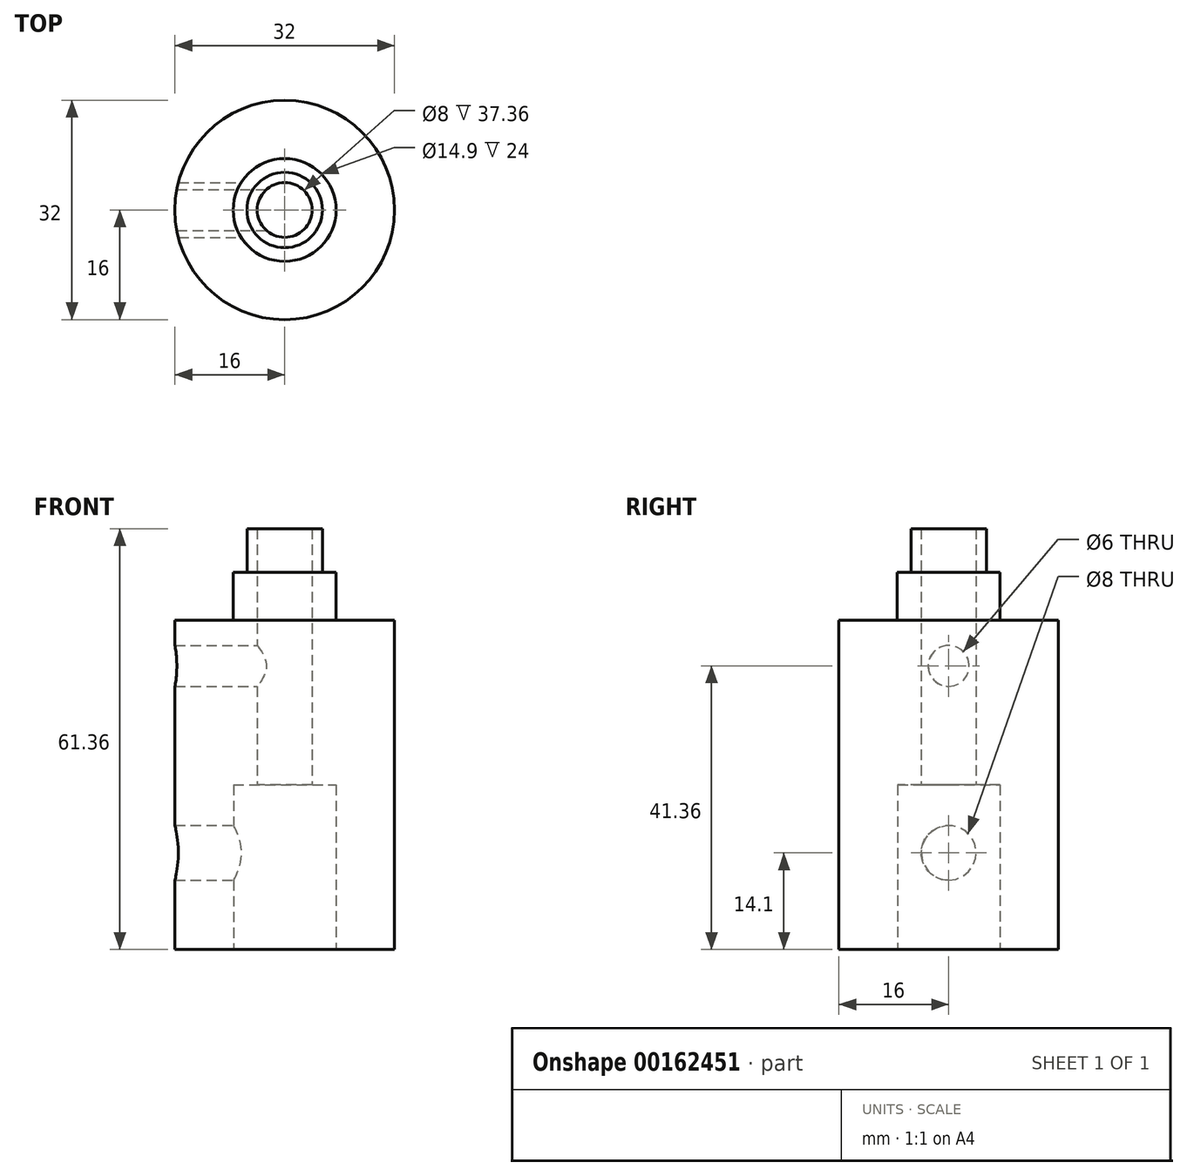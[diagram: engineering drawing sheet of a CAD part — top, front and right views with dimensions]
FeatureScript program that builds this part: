
annotation { "Feature Type Name" : "Feature", "Feature Type Description" : "" }
export const myFeature = defineFeature(function(context is Context, id is Id, definition is map)
    precondition{}
    {
        {
            var Q0;
            Q0=qCreatedBy(makeId("Top.planeOp"),FACE);
            var sketch = newSketch(context, id + "F0", { "sketchPlane" : qUnion([Q0])});
            skCircle(sketch, "E0", {"center": v(0, 0) * mm, "radius": 4 * mm});
            skCircle(sketch, "E1", {"center": v(0, 0) * mm, "radius": 5.5 * mm});
            skSolve(sketch);
        }
        {
            var Q0;
            Q0=makeQuery(id+"F0.imprint","IMPRINT",FACE,{"disambiguationData":[TD([[makeQuery(id+"F0.imprint","IMPRINT",EDGE,{"derivedFrom":sQuery(id+"F0.wireOp",EDGE,"E0")}),-1.0]])]});
            extrude(context, id + "F1", {"entities" : qUnion([Q0]), "depth" : (3 + (29 - 25.64)) * mm});
        }
        {
            var Q0;
            Q0=makeQuery(id+"F1.opExtrude","CAP_FACE",FACE,{"disambiguationData":[OSD([sQuery(id+"F0.wireOp",EDGE,"E0"),sQuery(id+"F0.wireOp",EDGE,"E1")])],"isStart":true});
            var sketch = newSketch(context, id + "F2", { "sketchPlane" : qUnion([Q0])});
            skCircle(sketch, "E2", {"center": v(0, 0) * mm, "radius": 4 * mm});
            skCircle(sketch, "E3", {"center": v(0, 0) * mm, "radius": 16 * mm});
            skSolve(sketch);
        }
        {
            var Q0;
            Q0=makeQuery(id+"F2.imprint","IMPRINT",FACE,{"disambiguationData":[TD([[makeQuery(id+"F2.imprint","IMPRINT",EDGE,{"derivedFrom":sQuery(id+"F2.wireOp",EDGE,"E2")}),1.0]])]});
            var Q1;
            Q1=makeQuery(id+"F2.imprint","IMPRINT",FACE,{"disambiguationData":[TD([[makeQuery(id+"F2.imprint","IMPRINT",EDGE,{"derivedFrom":sQuery(id+"F2.wireOp",EDGE,"E3")}),1.0]])]});
            extrude(context, id + "F3", {"entities" : qUnion([Q0, Q1]), "operationType" : NewBodyOperationType.ADD, "depth" : 55 * mm});
        }
        {
            var Q0;
            Q0=makeQuery(id+"F3.opExtrude","CAP_FACE",FACE,{"disambiguationData":[OSD([sQuery(id+"F2.wireOp",EDGE,"E2"),sQuery(id+"F2.wireOp",EDGE,"E3")])],"isStart":true});
            var sketch = newSketch(context, id + "F4", { "sketchPlane" : qUnion([Q0])});
            skCircle(sketch, "E4", {"center": v(0, 0) * mm, "radius": 7.5 * mm});
            skCircle(sketch, "E5", {"center": v(0, 0) * mm, "radius": 36.3 * mm});
            skSolve(sketch);
        }
        {
            var Q0;
            Q0=makeQuery(id+"F4.imprint","IMPRINT",FACE,{"disambiguationData":[TD([[makeQuery(id+"F4.imprint","IMPRINT",EDGE,{"derivedFrom":sQuery(id+"F4.wireOp",EDGE,"E5")}),1.0]])]});
            var Q1;
            Q1=makeQuery(id+"F4.imprint","IMPRINT",FACE,{"disambiguationData":[TD([[makeQuery(id+"F4.imprint","IMPRINT",EDGE,{"derivedFrom":sQuery(id+"F4.wireOp",EDGE,"E4")}),-1.0]])]});
            extrude(context, id + "F5", {"entities" : qUnion([Q0, Q1]), "operationType" : NewBodyOperationType.REMOVE, "oppositeDirection" : true, "depth" : 7 * mm});
        }
        {
            var Q0;
            Q0=qCreatedBy(makeId("Right.planeOp"),FACE);
            var sketch = newSketch(context, id + "F6", { "sketchPlane" : qUnion([Q0])});
            skCircle(sketch, "E6", {"center": v(0, -13.64) * mm, "radius": 3 * mm});
            skSolve(sketch);
        }
        {
            var Q0;
            Q0 = qSketchRegion(id + "F6", true);
            extrude(context, id + "F7", {"entities" : qUnion([Q0]), "operationType" : NewBodyOperationType.REMOVE, "oppositeDirection" : true, "depth" : 25 * mm});
        }
        {
            var Q0;
            Q0=makeQuery(id+"F3.opExtrude","CAP_FACE",FACE,{"disambiguationData":[OSD([sQuery(id+"F2.wireOp",EDGE,"E2"),sQuery(id+"F2.wireOp",EDGE,"E3")])],"isStart":false});
            var sketch = newSketch(context, id + "F8", { "sketchPlane" : qUnion([Q0])});
            skCircle(sketch, "E7", {"center": v(0, 0) * mm, "radius": 7.45 * mm});
            skSolve(sketch);
        }
        {
            var Q0;
            Q0=makeQuery(id+"F8.imprint","IMPRINT",FACE,{"disambiguationData":[TD([[makeQuery(id+"F8.imprint","IMPRINT",EDGE,{"derivedFrom":sQuery(id+"F8.wireOp",EDGE,"E7")}),1.0]])]});
            extrude(context, id + "F9", {"entities" : qUnion([Q0]), "operationType" : NewBodyOperationType.REMOVE, "oppositeDirection" : true, "depth" : 24 * mm});
        }
        {
            var Q0;
            Q0=qCreatedBy(makeId("Right.planeOp"),FACE);
            var sketch = newSketch(context, id + "F10", { "sketchPlane" : qUnion([Q0])});
            skCircle(sketch, "E8", {"center": v(0, -40.9) * mm, "radius": 4 * mm});
            skSolve(sketch);
        }
        {
            var Q0;
            Q0 = qSketchRegion(id + "F10", true);
            extrude(context, id + "F11", {"entities" : qUnion([Q0]), "operationType" : NewBodyOperationType.REMOVE, "oppositeDirection" : true, "depth" : 25 * mm});
        }
    });
